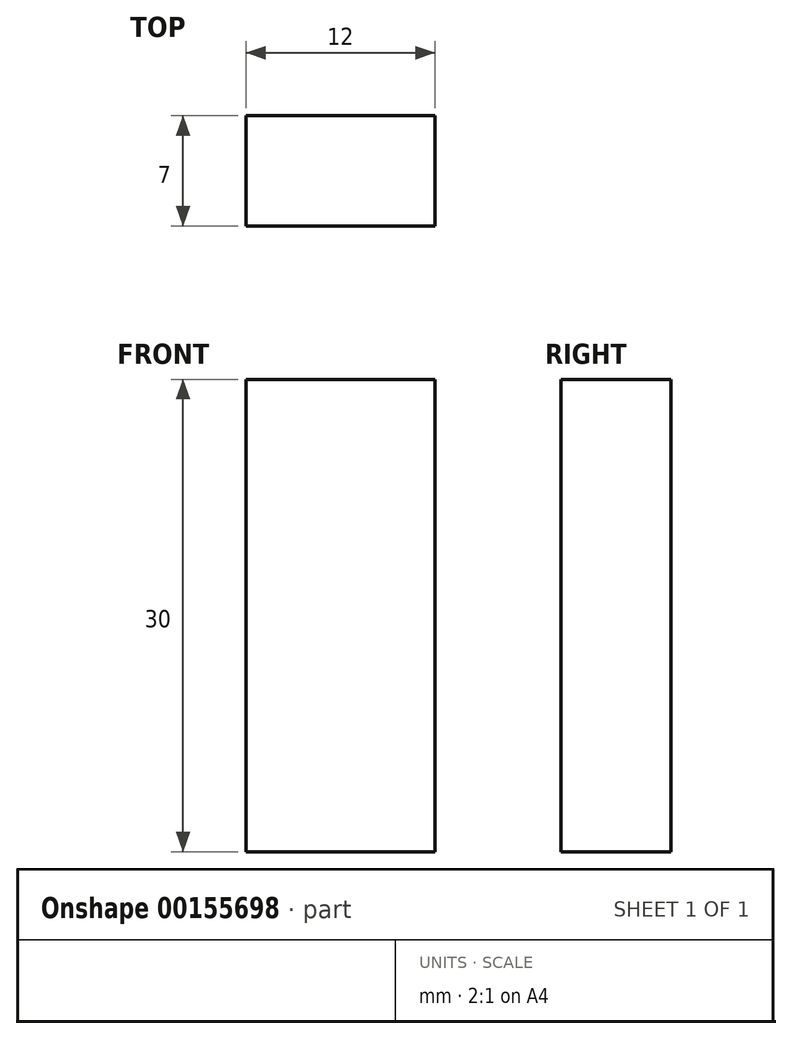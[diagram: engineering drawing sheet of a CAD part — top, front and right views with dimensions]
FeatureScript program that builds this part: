
annotation { "Feature Type Name" : "Feature", "Feature Type Description" : "" }
export const myFeature = defineFeature(function(context is Context, id is Id, definition is map)
    precondition{}
    {
        {
            var Q0;
            Q0=qCreatedBy(makeId("Front.planeOp"),FACE);
            var sketch = newSketch(context, id + "F0", { "sketchPlane" : qUnion([Q0])});
            skLineSegment(sketch, "E0.bottom", {"start": v(6, 15) * mm, "end": v(-6, 15) * mm});
            skLineSegment(sketch, "E0.top", {"start": v(6, -15) * mm, "end": v(-6, -15) * mm});
            skLineSegment(sketch, "E0.left", {"start": v(6, 15) * mm, "end": v(6, -15) * mm});
            skLineSegment(sketch, "E0.right", {"start": v(-6, 15) * mm, "end": v(-6, -15) * mm});
            skPoint(sketch, "E0.middle", {"position": v(0, 0) * mm});
            skSolve(sketch);
        }
        {
            var Q0;
            Q0=makeQuery(id+"F0.imprint","IMPRINT",FACE,{"disambiguationData":[TD([[makeQuery(id+"F0.imprint","IMPRINT",EDGE,{"derivedFrom":sQuery(id+"F0.wireOp",EDGE,"E0.bottom")}),1.0]])]});
            extrude(context, id + "F1", {"entities" : qUnion([Q0]), "endBound" : BoundingType.SYMMETRIC, "depth" : 7 * mm});
        }
    });
